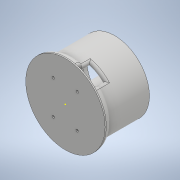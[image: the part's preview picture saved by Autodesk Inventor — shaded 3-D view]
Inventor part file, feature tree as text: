
AUTODESK INVENTOR PART (.ipt)
format: ipt  version: 2021 (Build 250183000, 183)  size: 646,656 bytes
history: native  units: mm
features: extrude x18, sketch x11, fillet x3, other x1, chamfer x1
ambient origin geometry x8: Origin, YZ Plane, XZ Plane, XY Plane, X Axis, Y Axis, Z Axis, Center Point
bodies: Body1 (feature_tree)
feature tree (34):
  other  "Sólido1"
  extrude  "Extrusión1"  Depth=144.0mm
  extrude  "Extrusión2"  Depth=100.0mm TaperAngle=0.0deg
  extrude  "Extrusión3"  Depth=124.0mm
  extrude  "Extrusión4"  Depth=104.0mm
  fillet  "Empalme1"  Radius=124.0mm
  extrude  "Extrusión5"  Depth=164.0mm
  extrude  "Extrusión6"  Depth=15.0mm TaperAngle=0.0deg
  extrude  "Extrusión7"  Depth=124.0mm
  extrude  "Extrusión8"  Depth=10.0mm TaperAngle=0.0deg
  extrude  "Extrusión9"  Depth=17.5mm TaperAngle=0.0deg
  extrude  "Extrusión10"  Depth=10.0mm TaperAngle=0.0deg
  extrude  "Extrusión11"  Depth=1.0mm
  extrude  "Extrusión12"  Depth=1.0mm TaperAngle=0.0deg
  extrude  "Extrusión13"  Depth=1.0mm
  extrude  "Extrusión14"  Depth=1.0mm TaperAngle=0.0deg
  sketch  "Boceto20"  dims[d26=30.0mm d27=0.0mm d30=10.0mm d31=0.0mm]
  sketch  "Boceto21"  dims[d32=8.0mm d33=0.0mm d34=17.5mm d35=0.0mm]
  extrude  "Extrusión15"  Depth=1.0mm TaperAngle=0.0deg
  sketch  "Boceto23"  dims[d36=10.0mm d37=0.0mm d38=67.25mm d39=0.0mm]
  extrude  "Extrusión16"  Depth=1.0mm TaperAngle=0.0deg
  extrude  "Extrusión17"  Depth=1.0mm TaperAngle=0.0deg
  fillet  "Empalme2"  Radius=2.0mm
  chamfer  "Chaflán1"  Distance=5.0mm
  extrude  "Extrusión18"  Depth=1.0mm TaperAngle=45.0deg
  fillet  "Empalme3"  Radius=10.0mm
  sketch  "Boceto1"  dims[d5=124.0mm d6=144.0mm]
  sketch  "Boceto5"  dims[d7=104.0mm d8=100.0mm d9=0.0mm]
  sketch  "Boceto6"  dims[d11=104.0mm d12=124.0mm]
  sketch  "Boceto7"  dims[d13=95.0mm d14=0.0mm d15=104.0mm d16=124.0mm]
  sketch  "Boceto10"  dims[d17=80.0mm d18=0.0mm d19=164.0mm]
  sketch  "Boceto17"  dims[d20=144.0mm d21=15.0mm d22=0.0mm]
  sketch  "Boceto18"  dims[d23=15.0mm d25=124.0mm]
  sketch  "Boceto25"  dims[d40=64.5mm d41=0.0mm d42=24.0mm d43=65.0mm d44=0.0mm d45=22.0mm d46=2.0mm d47=0.0mm d48=18.25mm d49=0.0mm d50=2.0mm d51=0.0mm d52=2.0mm d53=0.0mm d54=2.0mm d55=0.0mm d56=5.0mm d57=6.1mm d58=2.0mm d59=45.0deg d72=10.0mm d73=0.0mm d74=1.0mm d86=4.0mm d87=4.0mm d92=2.5mm d93=6.0mm d99=120.0mm d101=360.0deg d103=1.0mm]
